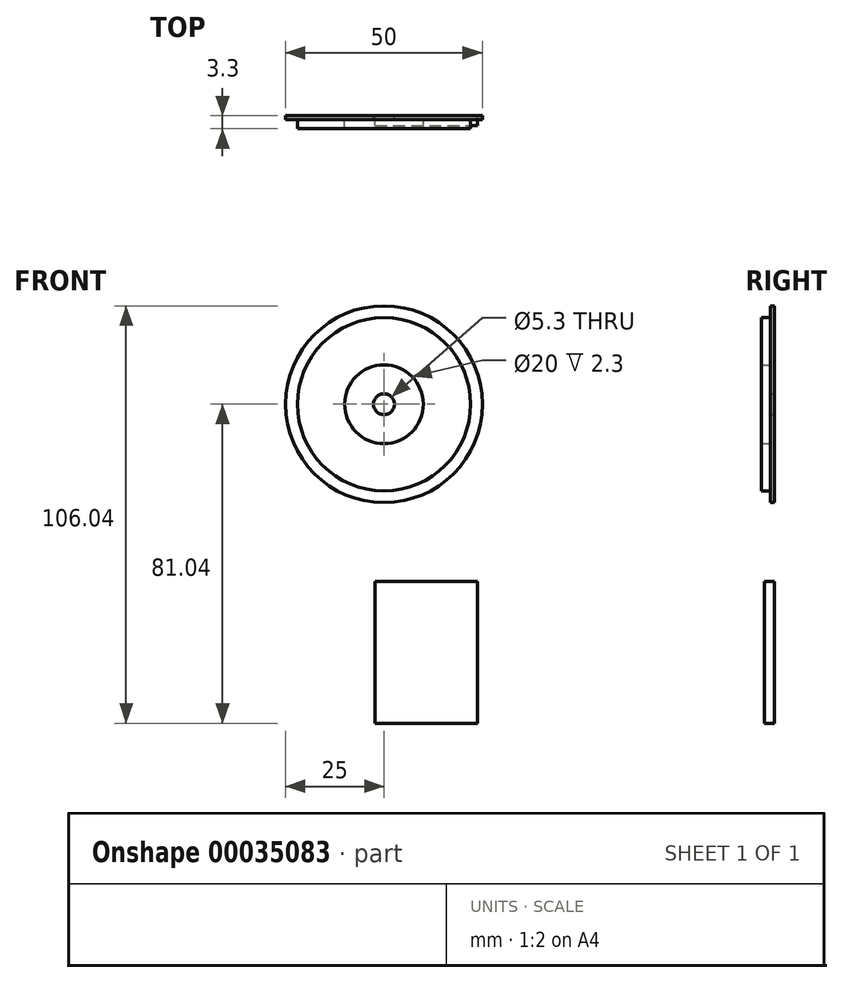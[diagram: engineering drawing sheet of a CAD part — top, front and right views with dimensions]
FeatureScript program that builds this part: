
annotation { "Feature Type Name" : "Feature", "Feature Type Description" : "" }
export const myFeature = defineFeature(function(context is Context, id is Id, definition is map)
    precondition{}
    {
        {
            var Q0;
            Q0=qCreatedBy(makeId("Front.planeOp"),FACE);
            var sketch = newSketch(context, id + "F0", { "sketchPlane" : qUnion([Q0])});
            skCircle(sketch, "E0", {"center": v(0, 0) * mm, "radius": 25 * mm});
            skCircle(sketch, "E1", {"center": v(0, 0) * mm, "radius": 22 * mm});
            skCircle(sketch, "E2", {"center": v(0, 0) * mm, "radius": 2.65 * mm});
            skCircle(sketch, "E3", {"center": v(0, 0) * mm, "radius": 10 * mm});
            skSolve(sketch);
        }
        {
            var Q0;
            Q0 = qSketchRegion(id + "F0", true);
            var Q1;
            Q1=makeQuery(id+"F0.imprint","IMPRINT",FACE,{"disambiguationData":[TD([[makeQuery(id+"F0.imprint","IMPRINT",EDGE,{"derivedFrom":sQuery(id+"F0.wireOp",EDGE,"E1")}),1.0]])]});
            var Q2;
            Q2=makeQuery(id+"F0.imprint","IMPRINT",FACE,{"disambiguationData":[TD([[makeQuery(id+"F0.imprint","IMPRINT",EDGE,{"derivedFrom":sQuery(id+"F0.wireOp",EDGE,"E2")}),-1.0]])]});
            extrude(context, id + "F1", {"entities" : qUnion([Q0, Q1, Q2]), "depth" : 1 * mm});
        }
        {
            var Q0;
            Q0=makeQuery(id+"F0.imprint","IMPRINT",FACE,{"disambiguationData":[TD([[makeQuery(id+"F0.imprint","IMPRINT",EDGE,{"derivedFrom":sQuery(id+"F0.wireOp",EDGE,"E1")}),1.0]])]});
            extrude(context, id + "F2", {"entities" : qUnion([Q0]), "operationType" : NewBodyOperationType.ADD, "depth" : 3.3 * mm});
        }
        {
            var Q0;
            Q0=qCreatedBy(makeId("Front.planeOp"),FACE);
            var sketch = newSketch(context, id + "F3", { "sketchPlane" : qUnion([Q0])});
            skLineSegment(sketch, "E4.bottom", {"start": v(-2.27, -45.04) * mm, "end": v(23.73, -45.04) * mm});
            skLineSegment(sketch, "E4.top", {"start": v(-2.27, -81.04) * mm, "end": v(23.73, -81.04) * mm});
            skLineSegment(sketch, "E4.left", {"start": v(-2.27, -45.04) * mm, "end": v(-2.27, -81.04) * mm});
            skLineSegment(sketch, "E4.right", {"start": v(23.73, -45.04) * mm, "end": v(23.73, -81.04) * mm});
            skLineSegment(sketch, "E5.bottom", {"start": v(3.22, -81.04) * mm, "end": v(15.22, -81.04) * mm});
            skLineSegment(sketch, "E5.top", {"start": v(3.22, -85.04) * mm, "end": v(15.22, -85.04) * mm});
            skLineSegment(sketch, "E5.left", {"start": v(3.22, -81.04) * mm, "end": v(3.22, -85.04) * mm});
            skLineSegment(sketch, "E5.right", {"start": v(15.22, -81.04) * mm, "end": v(15.22, -85.04) * mm});
            skSolve(sketch);
        }
        {
            var Q0;
            Q0=makeQuery(id+"F3.imprint","IMPRINT",FACE,{"disambiguationData":[TD([[makeQuery(id+"F3.imprint","IMPRINT",EDGE,{"derivedFrom":sQuery(id+"F3.wireOp",EDGE,"E5.bottom")}),-1.0]])]});
            var Q1;
            Q1=makeQuery(id+"F3.imprint","IMPRINT",FACE,{"disambiguationData":[TD([[makeQuery(id+"F3.imprint","IMPRINT",EDGE,{"derivedFrom":sQuery(id+"F3.wireOp",EDGE,"E4.bottom")}),-1.0]])]});
            extrude(context, id + "F4", {"entities" : qUnion([Q0, Q1]), "depth" : 2.5 * mm});
        }
    });
